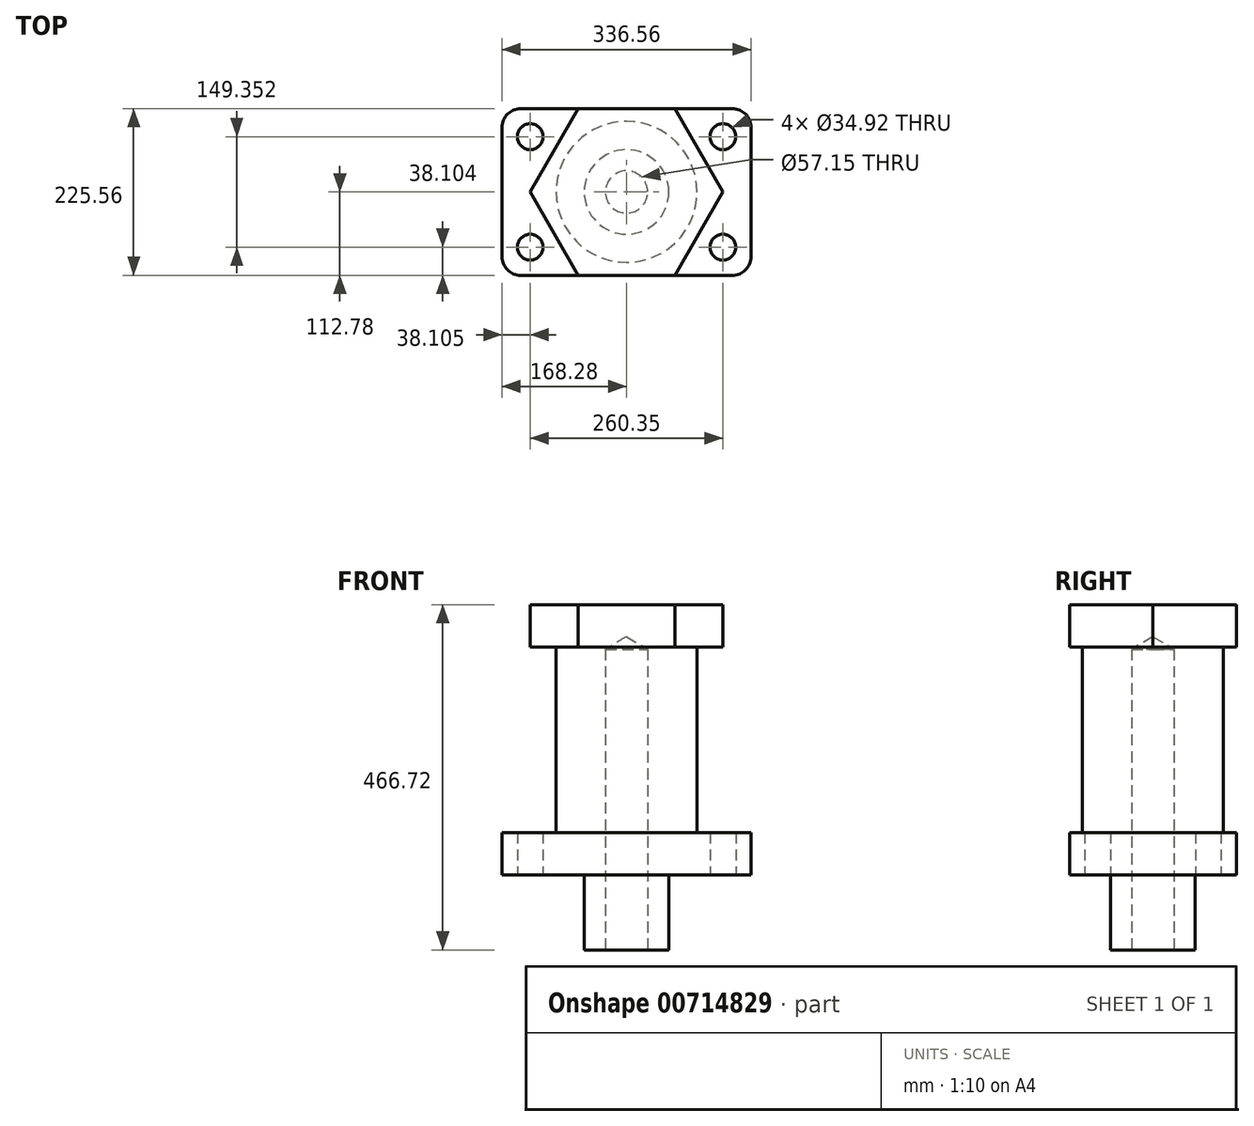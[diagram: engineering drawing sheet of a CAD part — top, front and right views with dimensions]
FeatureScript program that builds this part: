
annotation { "Feature Type Name" : "Feature", "Feature Type Description" : "" }
export const myFeature = defineFeature(function(context is Context, id is Id, definition is map)
    precondition{}
    {
        {
            var Q0;
            Q0=qCreatedBy(makeId("Top.planeOp"),FACE);
            var sketch = newSketch(context, id + "F0", { "sketchPlane" : qUnion([Q0])});
            skLineSegment(sketch, "E0.bottom", {"start": v(-142.87, 112.71) * mm, "end": v(142.88, 112.71) * mm});
            skLineSegment(sketch, "E0.top", {"start": v(-142.88, -112.71) * mm, "end": v(142.88, -112.71) * mm});
            skLineSegment(sketch, "E0.left", {"start": v(-168.27, 87.31) * mm, "end": v(-168.28, -87.31) * mm});
            skLineSegment(sketch, "E0.right", {"start": v(168.28, 87.31) * mm, "end": v(168.28, -87.31) * mm});
            skPoint(sketch, "E0.middle", {"position": v(0, 0) * mm});
            skPoint(sketch, "E1.visualSharp", {"position": v(-168.27, 112.71) * mm});
            skArc(sketch, "E1.filletArc", {"start": v(-142.87, 112.71) * mm, "mid": v(-160.84, 105.27) * mm, "end": v(-168.27, 87.31) * mm});
            skPoint(sketch, "E2.visualSharp", {"position": v(168.28, 112.71) * mm});
            skArc(sketch, "E2.filletArc", {"start": v(168.28, 87.31) * mm, "mid": v(160.84, 105.27) * mm, "end": v(142.88, 112.71) * mm});
            skPoint(sketch, "E3.visualSharp", {"position": v(168.28, -112.71) * mm});
            skArc(sketch, "E3.filletArc", {"start": v(142.88, -112.71) * mm, "mid": v(160.84, -105.27) * mm, "end": v(168.28, -87.31) * mm});
            skPoint(sketch, "E4.visualSharp", {"position": v(-168.28, -112.71) * mm});
            skArc(sketch, "E4.filletArc", {"start": v(-168.28, -87.31) * mm, "mid": v(-160.84, -105.27) * mm, "end": v(-142.88, -112.71) * mm});
            skSolve(sketch);
        }
        {
            var Q0;
            Q0 = qSketchRegion(id + "F0", true);
            extrude(context, id + "F1", {"entities" : qUnion([Q0]), "depth" : 57.15 * mm, "offsetDistance" : 25.4 * mm});
        }
        {
            var Q0;
            Q0=makeQuery(id+"F1.opExtrude","CAP_FACE",FACE,{"disambiguationData":[OSD([sQuery(id+"F0.wireOp",EDGE,"E0.bottom"),sQuery(id+"F0.wireOp",EDGE,"E0.top"),sQuery(id+"F0.wireOp",EDGE,"E0.left"),sQuery(id+"F0.wireOp",EDGE,"E0.right"),sQuery(id+"F0.wireOp",EDGE,"E1.filletArc"),sQuery(id+"F0.wireOp",EDGE,"E2.filletArc"),sQuery(id+"F0.wireOp",EDGE,"E3.filletArc"),sQuery(id+"F0.wireOp",EDGE,"E4.filletArc")])],"isStart":false});
            var sketch = newSketch(context, id + "F2", { "sketchPlane" : qUnion([Q0])});
            skCircle(sketch, "E5", {"center": v(0, 0) * mm, "radius": 95.25 * mm});
            skSolve(sketch);
        }
        {
            var Q0;
            Q0 = qSketchRegion(id + "F2", true);
            extrude(context, id + "F3", {"entities" : qUnion([Q0]), "operationType" : NewBodyOperationType.ADD, "depth" : 250.82 * mm, "offsetDistance" : 25.4 * mm});
        }
        {
            var Q0;
            Q0=makeQuery(id+"F3.opExtrude","CAP_FACE",FACE,{"disambiguationData":[OSD([sQuery(id+"F2.wireOp",EDGE,"E5")])],"isStart":false});
            var sketch = newSketch(context, id + "F4", { "sketchPlane" : qUnion([Q0])});
            skCircle(sketch, "E6.cCircle", {"center": v(0, 0) * mm, "radius": 112.78 * mm, "construction": true});
            skLineSegment(sketch, "E6.0", {"start": v(-65.11, 112.78) * mm, "end": v(65.11, 112.78) * mm});
            skLineSegment(sketch, "E6.1", {"start": v(65.11, 112.78) * mm, "end": v(130.23, 0) * mm});
            skLineSegment(sketch, "E6.2", {"start": v(130.23, 0) * mm, "end": v(65.11, -112.78) * mm});
            skLineSegment(sketch, "E6.3", {"start": v(65.11, -112.78) * mm, "end": v(-65.11, -112.78) * mm});
            skLineSegment(sketch, "E6.4", {"start": v(-65.11, -112.78) * mm, "end": v(-130.23, 0) * mm});
            skLineSegment(sketch, "E6.5", {"start": v(-130.23, 0) * mm, "end": v(-65.11, 112.78) * mm});
            skPoint(sketch, "E6.0.midPoint", {"position": v(0, 112.78) * mm});
            skSolve(sketch);
        }
        {
            var Q0;
            Q0 = qSketchRegion(id + "F4", true);
            extrude(context, id + "F5", {"entities" : qUnion([Q0]), "operationType" : NewBodyOperationType.ADD, "depth" : 57.15 * mm, "offsetDistance" : 25.4 * mm});
        }
        {
            var Q0;
            Q0=makeQuery(id+"F1.opExtrude","CAP_FACE",FACE,{"disambiguationData":[OSD([sQuery(id+"F0.wireOp",EDGE,"E0.bottom"),sQuery(id+"F0.wireOp",EDGE,"E0.top"),sQuery(id+"F0.wireOp",EDGE,"E0.left"),sQuery(id+"F0.wireOp",EDGE,"E0.right"),sQuery(id+"F0.wireOp",EDGE,"E1.filletArc"),sQuery(id+"F0.wireOp",EDGE,"E2.filletArc"),sQuery(id+"F0.wireOp",EDGE,"E3.filletArc"),sQuery(id+"F0.wireOp",EDGE,"E4.filletArc")])],"isStart":true});
            var sketch = newSketch(context, id + "F6", { "sketchPlane" : qUnion([Q0])});
            skLineSegment(sketch, "E7.bottom", {"start": v(-130.18, 74.68) * mm, "end": v(130.18, 74.68) * mm, "construction": true});
            skLineSegment(sketch, "E7.top", {"start": v(-130.18, -74.68) * mm, "end": v(130.17, -74.68) * mm, "construction": true});
            skLineSegment(sketch, "E7.left", {"start": v(-130.18, 74.68) * mm, "end": v(-130.18, -74.68) * mm, "construction": true});
            skLineSegment(sketch, "E7.right", {"start": v(130.18, 74.68) * mm, "end": v(130.17, -74.68) * mm, "construction": true});
            skPoint(sketch, "E7.middle", {"position": v(0, 0) * mm});
            skPoint(sketch, "E8", {"position": v(-130.18, 74.68) * mm});
            skPoint(sketch, "E9", {"position": v(130.18, 74.68) * mm});
            skPoint(sketch, "E10", {"position": v(130.17, -74.68) * mm});
            skPoint(sketch, "E11", {"position": v(-130.18, -74.68) * mm});
            skSolve(sketch);
        }
        {
            var Q0;
            Q0=sQuery(id+"F6.wireOp",VERTEX,"E8");
            var Q1;
            Q1=sQuery(id+"F6.wireOp",VERTEX,"E11");
            var Q2;
            Q2=sQuery(id+"F6.wireOp",VERTEX,"E10");
            var Q3;
            Q3=sQuery(id+"F6.wireOp",VERTEX,"E9");
            var Q4;
            Q4=makeQuery(id+"F1.opExtrude","SWEPT_BODY",BODY,{"disambiguationData":[OSD([sQuery(id+"F0.wireOp",EDGE,"E0.bottom"),sQuery(id+"F0.wireOp",EDGE,"E0.top"),sQuery(id+"F0.wireOp",EDGE,"E0.left"),sQuery(id+"F0.wireOp",EDGE,"E0.right"),sQuery(id+"F0.wireOp",EDGE,"E1.filletArc"),sQuery(id+"F0.wireOp",EDGE,"E2.filletArc"),sQuery(id+"F0.wireOp",EDGE,"E3.filletArc"),sQuery(id+"F0.wireOp",EDGE,"E4.filletArc")])]});
            hole(context, id + "F7", {"style" : HoleStyle.SIMPLE, "endStyle" : HoleEndStyle.THROUGH, "holeDiameter" : 34.92 * mm, "majorDiameter" : 6.35 * mm, "isTappedThrough" : true, "tappedDepth" : 34.3 * mm, "tapClearance" : 3, "locations" : qUnion([Q0, Q1, Q2, Q3]), "scope" : qUnion([Q4])});
        }
        {
            var Q0;
            Q0=makeQuery(id+"F1.opExtrude","CAP_FACE",FACE,{"disambiguationData":[OSD([sQuery(id+"F0.wireOp",EDGE,"E0.bottom"),sQuery(id+"F0.wireOp",EDGE,"E0.top"),sQuery(id+"F0.wireOp",EDGE,"E0.left"),sQuery(id+"F0.wireOp",EDGE,"E0.right"),sQuery(id+"F0.wireOp",EDGE,"E1.filletArc"),sQuery(id+"F0.wireOp",EDGE,"E2.filletArc"),sQuery(id+"F0.wireOp",EDGE,"E3.filletArc"),sQuery(id+"F0.wireOp",EDGE,"E4.filletArc")])],"isStart":true});
            var sketch = newSketch(context, id + "F8", { "sketchPlane" : qUnion([Q0])});
            skCircle(sketch, "E12", {"center": v(0, 0) * mm, "radius": 57.15 * mm});
            skSolve(sketch);
        }
        {
            var Q0;
            Q0 = qSketchRegion(id + "F8", true);
            extrude(context, id + "F9", {"entities" : qUnion([Q0]), "operationType" : NewBodyOperationType.ADD, "depth" : 101.6 * mm, "offsetDistance" : 25.4 * mm});
        }
        {
            var Q0;
            Q0=makeQuery(id+"F9.opExtrude","CAP_FACE",FACE,{"disambiguationData":[OSD([sQuery(id+"F8.wireOp",EDGE,"E12")])],"isStart":false});
            var sketch = newSketch(context, id + "F10", { "sketchPlane" : qUnion([Q0])});
            skPoint(sketch, "E13", {"position": v(0, 0) * mm});
            skSolve(sketch);
        }
        {
            var Q0;
            Q0=sQuery(id+"F10.wireOp",VERTEX,"E13");
            var Q1;
            Q1=makeQuery(id+"F1.opExtrude","SWEPT_BODY",BODY,{"disambiguationData":[OSD([sQuery(id+"F0.wireOp",EDGE,"E0.bottom"),sQuery(id+"F0.wireOp",EDGE,"E0.top"),sQuery(id+"F0.wireOp",EDGE,"E0.left"),sQuery(id+"F0.wireOp",EDGE,"E0.right"),sQuery(id+"F0.wireOp",EDGE,"E1.filletArc"),sQuery(id+"F0.wireOp",EDGE,"E2.filletArc"),sQuery(id+"F0.wireOp",EDGE,"E3.filletArc"),sQuery(id+"F0.wireOp",EDGE,"E4.filletArc")])]});
            hole(context, id + "F11", {"style" : HoleStyle.SIMPLE, "endStyle" : HoleEndStyle.BLIND, "holeDiameter" : 57.15 * mm, "majorDiameter" : 6.35 * mm, "holeDepth" : 406.4 * mm, "isTappedThrough" : true, "tappedDepth" : 34.3 * mm, "tapClearance" : 3, "locations" : qUnion([Q0]), "scope" : qUnion([Q1])});
        }
    });
